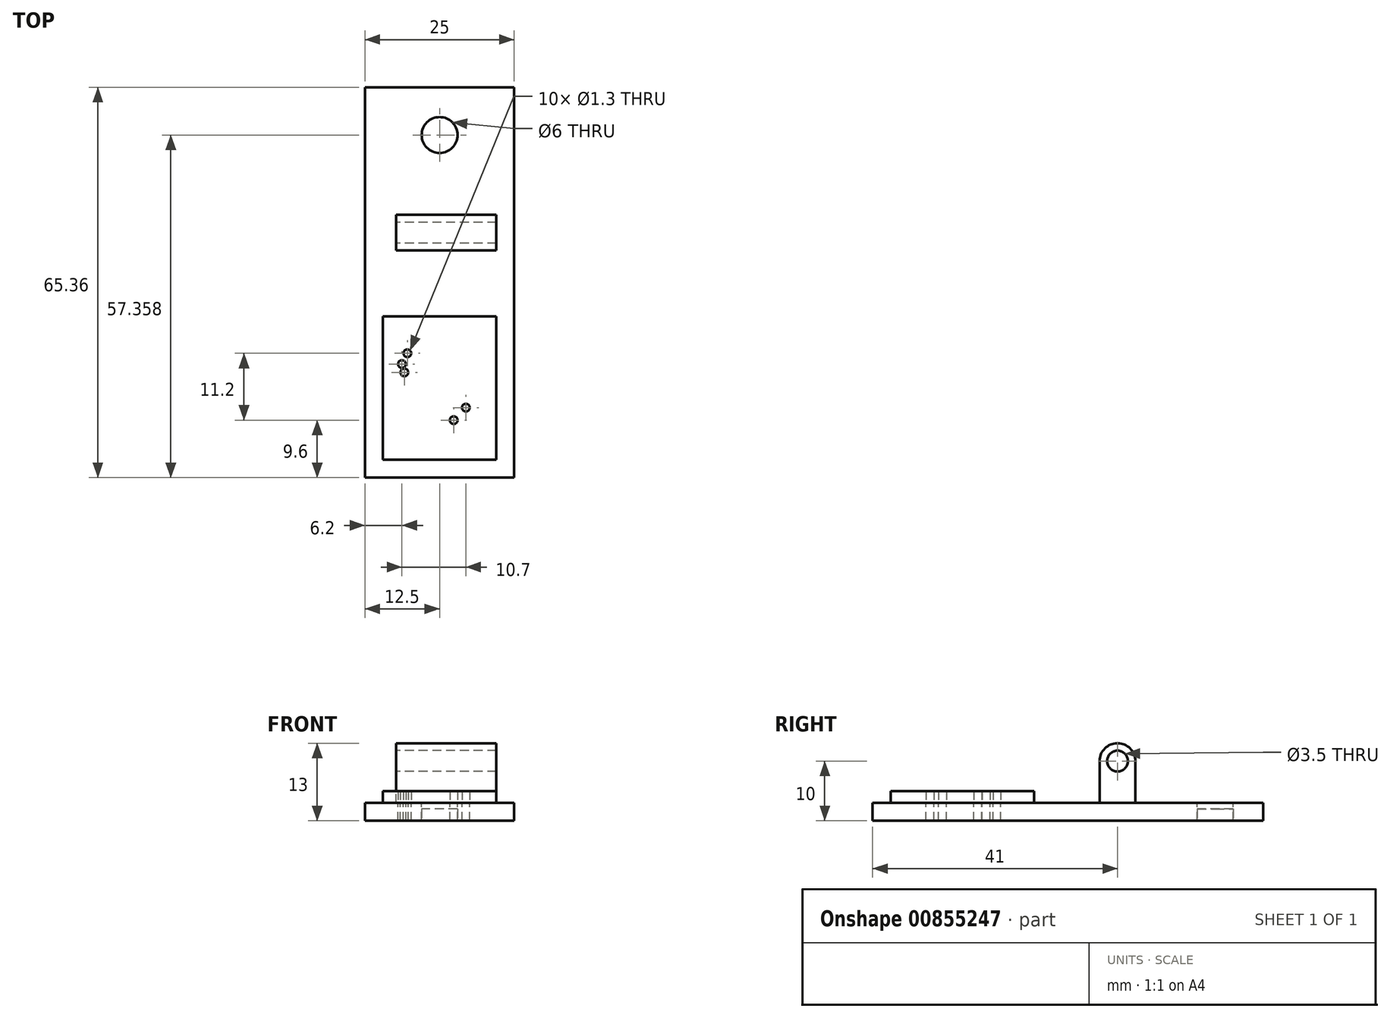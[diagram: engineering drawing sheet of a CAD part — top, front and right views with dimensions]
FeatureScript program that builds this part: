
annotation { "Feature Type Name" : "Feature", "Feature Type Description" : "" }
export const myFeature = defineFeature(function(context is Context, id is Id, definition is map)
    precondition{}
    {
        {
            var Q0;
            Q0=qCreatedBy(makeId("Top.planeOp"),FACE);
            var sketch = newSketch(context, id + "F0", { "sketchPlane" : qUnion([Q0])});
            skLineSegment(sketch, "E0.bottom", {"start": v(0, 0) * mm, "end": v(-19, 0) * mm});
            skLineSegment(sketch, "E0.top", {"start": v(0, 24) * mm, "end": v(-19, 24) * mm});
            skLineSegment(sketch, "E0.left", {"start": v(0, 0) * mm, "end": v(0, 24) * mm});
            skLineSegment(sketch, "E0.right", {"start": v(-19, 0) * mm, "end": v(-19, 24) * mm});
            skLineSegment(sketch, "E1.0", {"start": v(3, 27) * mm, "end": v(-22, 27) * mm});
            skLineSegment(sketch, "E1.1", {"start": v(3, -3) * mm, "end": v(3, 27) * mm});
            skLineSegment(sketch, "E1.2", {"start": v(3, -3) * mm, "end": v(-22, -3) * mm});
            skLineSegment(sketch, "E1.3", {"start": v(-22, -3) * mm, "end": v(-22, 27) * mm});
            skLineSegment(sketch, "E2.bottom", {"start": v(-19, 0) * mm, "end": v(-15.95, 0) * mm});
            skLineSegment(sketch, "E2.top", {"start": v(-19, -3) * mm, "end": v(-15.95, -3) * mm});
            skLineSegment(sketch, "E2.left", {"start": v(-19, 0) * mm, "end": v(-19, -3) * mm});
            skLineSegment(sketch, "E2.right", {"start": v(-15.95, 0) * mm, "end": v(-15.95, -3) * mm});
            skLineSegment(sketch, "E3.bottom", {"start": v(-4.14, 0) * mm, "end": v(0, 0) * mm});
            skLineSegment(sketch, "E3.top", {"start": v(-4.14, -3) * mm, "end": v(0, -3) * mm});
            skLineSegment(sketch, "E3.left", {"start": v(-4.14, 0) * mm, "end": v(-4.14, -3) * mm});
            skLineSegment(sketch, "E3.right", {"start": v(0, 0) * mm, "end": v(0, -3) * mm});
            skLineSegment(sketch, "E4.bottom", {"start": v(-19, 24) * mm, "end": v(0, 24) * mm});
            skLineSegment(sketch, "E4.top", {"start": v(-19, 10.13) * mm, "end": v(0, 10.13) * mm});
            skLineSegment(sketch, "E4.left", {"start": v(-19, 24) * mm, "end": v(-19, 10.13) * mm});
            skLineSegment(sketch, "E4.right", {"start": v(0, 24) * mm, "end": v(0, 10.13) * mm});
            skLineSegment(sketch, "E5.bottom", {"start": v(-10.54, 0) * mm, "end": v(-4.14, 0) * mm});
            skLineSegment(sketch, "E5.top", {"start": v(-10.54, -3) * mm, "end": v(-4.14, -3) * mm});
            skLineSegment(sketch, "E5.left", {"start": v(-10.54, 0) * mm, "end": v(-10.54, -3) * mm});
            skLineSegment(sketch, "E6.bottom", {"start": v(-22, 27) * mm, "end": v(3, 27) * mm});
            skLineSegment(sketch, "E6.top", {"start": v(-22, 62.36) * mm, "end": v(3, 62.36) * mm});
            skLineSegment(sketch, "E6.left", {"start": v(-22, 27) * mm, "end": v(-22, 62.36) * mm});
            skLineSegment(sketch, "E6.right", {"start": v(3, 27) * mm, "end": v(3, 62.36) * mm});
            skCircle(sketch, "E7", {"center": v(-7.14, 6.6) * mm, "radius": 0.65 * mm});
            skCircle(sketch, "E8", {"center": v(-5.1, 8.7) * mm, "radius": 0.65 * mm});
            skCircle(sketch, "E9", {"center": v(-14.9, 17.8) * mm, "radius": 0.65 * mm});
            skCircle(sketch, "E10", {"center": v(-15.8, 16) * mm, "radius": 0.65 * mm});
            skCircle(sketch, "E11", {"center": v(-15.4, 14.6) * mm, "radius": 0.65 * mm});
            skCircle(sketch, "E12", {"center": v(-9.5, 54.36) * mm, "radius": 3 * mm});
            skSolve(sketch);
        }
        {
            var Q0;
            {var subQ0=sQuery(id+"F0.wireOp",EDGE,"E2.right");var subQ8=makeQuery(id+"F0.imprint","IMPRINT",EDGE,{"derivedFrom":subQ0});var subQ11=makeQuery(id+"F0.imprint","IMPRINT",EDGE,{"derivedFrom":sQuery(id+"F0.wireOp",EDGE,"E1.0")});var subQ12=sQuery(id+"F0.wireOp",EDGE,"E2.left");var subQ19=sQuery(id+"F0.wireOp",EDGE,"E0.top");var subQ25=makeQuery(id+"F0.imprint","IMPRINT",EDGE,{"derivedFrom":subQ12});var subQ27=sQuery(id+"F0.wireOp",EDGE,"E3.left");var subQ29=makeQuery(id+"F0.imprint","IMPRINT",EDGE,{"derivedFrom":subQ27});Q0=qUnion([makeQuery(id+"F0.imprint","IMPRINT",FACE,{"disambiguationData":[TD([[subQ29,1.0]])]}),makeQuery(id+"F0.imprint","IMPRINT",FACE,{"disambiguationData":[TD([[subQ11,-1.0]])]}),makeQuery(id+"F0.imprint","IMPRINT",FACE,{"disambiguationData":[TD([[subQ25,1.0]])]}),makeQuery(id+"F0.imprint","IMPRINT",FACE,{"disambiguationData":[TD([[subQ29,-1.0]])]}),makeQuery(id+"F0.imprint","IMPRINT",FACE,{"disambiguationData":[TD([[makeQuery(id+"F0.imprint","IMPRINT",EDGE,{"derivedFrom":subQ19}),-1.0]])]}),makeQuery(id+"F0.imprint","IMPRINT",FACE,{"disambiguationData":[TD([[subQ8,1.0]])]})]);}
            var Q1;
            {var subQ2=sQuery(id+"F0.wireOp",EDGE,"E0.top");Q1=makeQuery(id+"F0.imprint","IMPRINT",FACE,{"disambiguationData":[TD([[makeQuery(id+"F0.imprint","IMPRINT",EDGE,{"derivedFrom":subQ2}),1.0]])]});}
            var Q2;
            {var subQ8=sQuery(id+"F0.wireOp",EDGE,"E4.top");Q2=makeQuery(id+"F0.imprint","IMPRINT",FACE,{"disambiguationData":[TD([[makeQuery(id+"F0.imprint","IMPRINT",EDGE,{"derivedFrom":subQ8}),-1.0]])]});}
            extrude(context, id + "F1", {"entities" : qUnion([Q0, Q1, Q2]), "oppositeDirection" : true, "depth" : 3 * mm, "offsetDistance" : 25 * mm});
        }
        {
            var Q0;
            {var subQ2=sQuery(id+"F0.wireOp",EDGE,"E0.top");Q0=makeQuery(id+"F0.imprint","IMPRINT",FACE,{"disambiguationData":[TD([[makeQuery(id+"F0.imprint","IMPRINT",EDGE,{"derivedFrom":subQ2}),1.0]])]});}
            var Q1;
            {var subQ8=sQuery(id+"F0.wireOp",EDGE,"E4.top");Q1=makeQuery(id+"F0.imprint","IMPRINT",FACE,{"disambiguationData":[TD([[makeQuery(id+"F0.imprint","IMPRINT",EDGE,{"derivedFrom":subQ8}),-1.0]])]});}
            extrude(context, id + "F2", {"entities" : qUnion([Q0, Q1]), "depth" : 2 * mm, "offsetDistance" : 25 * mm});
        }
        {
            var Q0;
            Q0=makeQuery(id+"F1.opExtrude","SWEPT_FACE",FACE,{"disambiguationData":[OSD([sQuery(id+"F0.wireOp",EDGE,"E1.3"),sQuery(id+"F0.wireOp",EDGE,"E6.left")])]});
            var sketch = newSketch(context, id + "F3", { "sketchPlane" : qUnion([Q0])});
            skLineSegment(sketch, "E13.bottom", {"start": v(-41, 0) * mm, "end": v(-35, 0) * mm});
            skLineSegment(sketch, "E13.top", {"start": v(-41, 4) * mm, "end": v(-35, 4) * mm});
            skLineSegment(sketch, "E13.left", {"start": v(-41, 0) * mm, "end": v(-41, 4) * mm});
            skLineSegment(sketch, "E13.right", {"start": v(-35, 0) * mm, "end": v(-35, 4) * mm});
            skArc(sketch, "E14", {"start": v(-35, 4) * mm, "mid": v(-38, 7) * mm, "end": v(-41, 4) * mm});
            skCircle(sketch, "E15", {"center": v(-38, 4) * mm, "radius": 1.5 * mm});
            skSolve(sketch);
        }
        {
            var Q0;
            {var subQ2=sQuery(id+"F3.wireOp",EDGE,"E13.bottom");Q0=makeQuery(id+"F3.imprint","IMPRINT",FACE,{"disambiguationData":[TD([[makeQuery(id+"F3.imprint","IMPRINT",EDGE,{"derivedFrom":subQ2}),1.0]])]});}
            cPlane(context, id + "F4", {"entities" : qUnion([Q0]), "cplaneType" : CPlaneType.OFFSET, "offset" : 5.2 * mm, "oppositeDirection" : true, "width" : 150 * mm, "height" : 150 * mm});
        }
        {
            var Q0;
            Q0=qCreatedBy(id+"F4.planeOp",FACE);
            var sketch = newSketch(context, id + "F5", { "sketchPlane" : qUnion([Q0])});
            skLineSegment(sketch, "E16.bottom", {"start": v(-41, 0) * mm, "end": v(-35, 0) * mm});
            skLineSegment(sketch, "E16.top", {"start": v(-41, 7) * mm, "end": v(-35, 7) * mm});
            skLineSegment(sketch, "E16.left", {"start": v(-41, 0) * mm, "end": v(-41, 7) * mm});
            skLineSegment(sketch, "E16.right", {"start": v(-35, 0) * mm, "end": v(-35, 7) * mm});
            skArc(sketch, "E17", {"start": v(-35, 7) * mm, "mid": v(-38, 10) * mm, "end": v(-41, 7) * mm});
            skCircle(sketch, "E18", {"center": v(-38, 7) * mm, "radius": 1.75 * mm});
            skSolve(sketch);
        }
        {
            var Q0;
            {var subQ0=sQuery(id+"F5.wireOp",EDGE,"E17");Q0=makeQuery(id+"F5.imprint","IMPRINT",FACE,{"disambiguationData":[TD([[makeQuery(id+"F5.imprint","IMPRINT",EDGE,{"derivedFrom":subQ0}),1.0]])]});}
            var Q1;
            Q1=makeQuery(id+"F5.imprint","IMPRINT",FACE,{"disambiguationData":[TD([[makeQuery(id+"F5.imprint","IMPRINT",EDGE,{"derivedFrom":sQuery(id+"F5.wireOp",EDGE,"E16.bottom")}),1.0]])]});
            extrude(context, id + "F6", {"entities" : qUnion([Q0, Q1]), "operationType" : NewBodyOperationType.ADD, "oppositeDirection" : true, "depth" : 15.5 * mm, "offsetDistance" : 25 * mm});
        }
        {
            var Q0;
            Q0=makeQuery(id+"F1.opExtrude","CAP_FACE",FACE,{"disambiguationData":[OSD([sQuery(id+"F0.wireOp",EDGE,"E1.1"),sQuery(id+"F0.wireOp",EDGE,"E1.2"),sQuery(id+"F0.wireOp",EDGE,"E1.3"),sQuery(id+"F0.wireOp",EDGE,"E6.top"),sQuery(id+"F0.wireOp",EDGE,"E6.left"),sQuery(id+"F0.wireOp",EDGE,"E6.right"),sQuery(id+"F0.wireOp",EDGE,"E7"),sQuery(id+"F0.wireOp",EDGE,"E8"),sQuery(id+"F0.wireOp",EDGE,"E9"),sQuery(id+"F0.wireOp",EDGE,"E10"),sQuery(id+"F0.wireOp",EDGE,"E11"),sQuery(id+"F0.wireOp",EDGE,"E12")])],"isStart":false});
            var sketch = newSketch(context, id + "F7", { "sketchPlane" : qUnion([Q0])});
            skCircle(sketch, "E19", {"center": v(-9.5, -54.36) * mm, "radius": 3 * mm});
            skSolve(sketch);
        }
        {
            var Q0;
            Q0=makeQuery(id+"F7.imprint","IMPRINT",FACE,{"disambiguationData":[TD([[makeQuery(id+"F7.imprint","IMPRINT",EDGE,{"derivedFrom":sQuery(id+"F7.wireOp",EDGE,"E19")}),-1.0]])]});
            extrude(context, id + "F8", {"entities" : qUnion([Q0]), "oppositeDirection" : true, "depth" : 2 * mm, "offsetDistance" : 25 * mm});
        }
        {
            var Q0;
            Q0=makeQuery(id+"F6.opExtrude","CAP_FACE",FACE,{"disambiguationData":[OSD([sQuery(id+"F5.wireOp",EDGE,"E16.bottom"),sQuery(id+"F5.wireOp",EDGE,"E16.left"),sQuery(id+"F5.wireOp",EDGE,"E16.right"),sQuery(id+"F5.wireOp",EDGE,"E17"),sQuery(id+"F5.wireOp",EDGE,"E18")])],"isStart":false});
            extrude(context, id + "F9", {"entities" : qUnion([Q0]), "operationType" : NewBodyOperationType.ADD, "depth" : 1.3 * mm, "offsetDistance" : 25 * mm});
        }
    });
